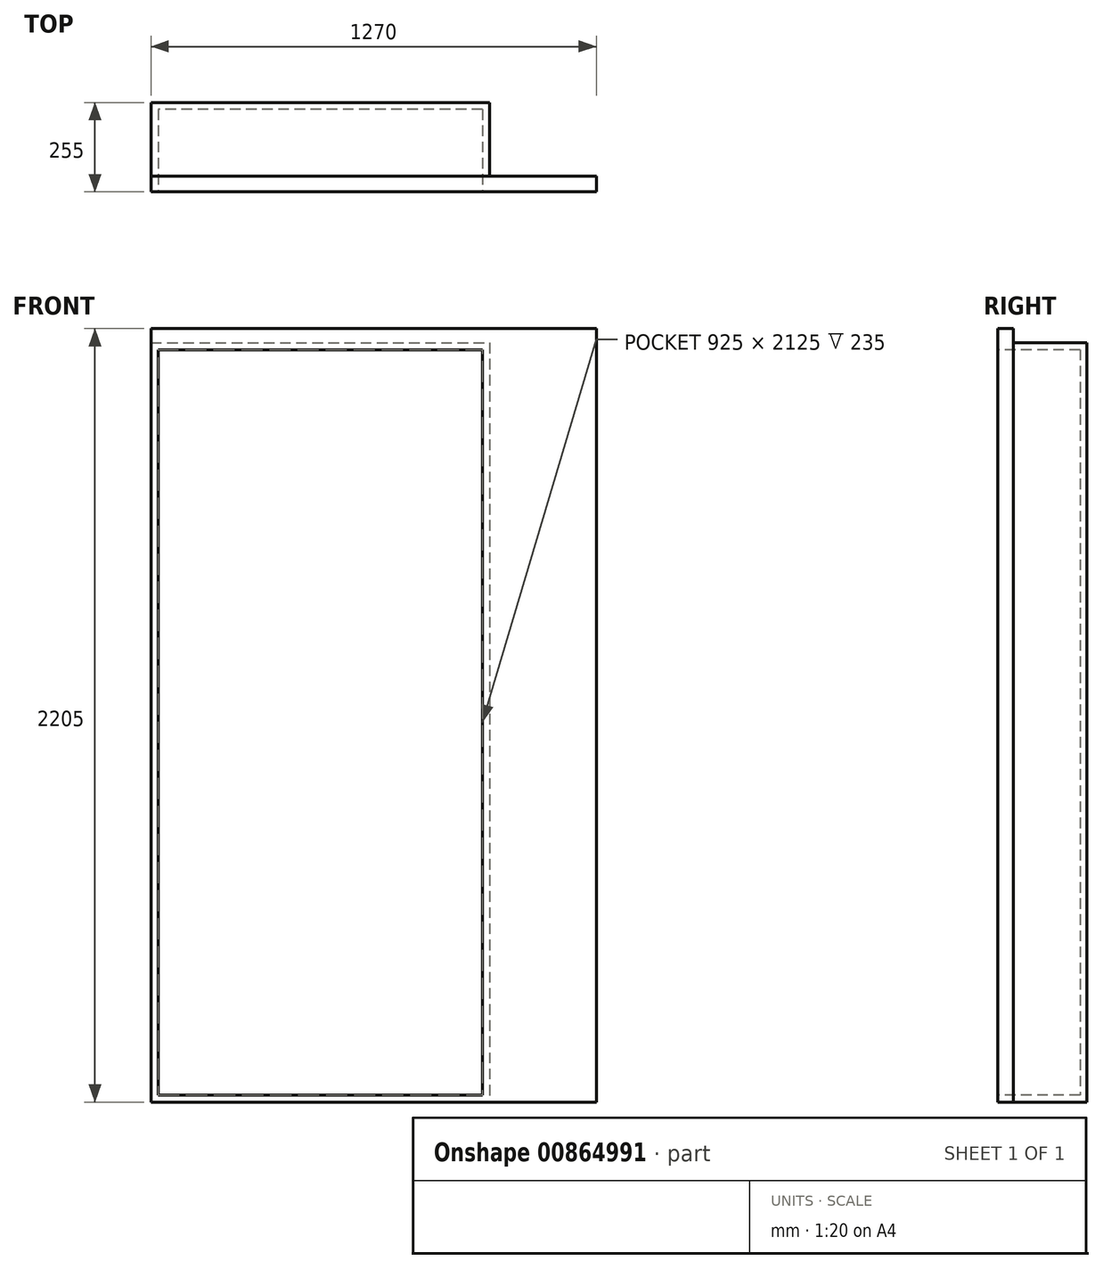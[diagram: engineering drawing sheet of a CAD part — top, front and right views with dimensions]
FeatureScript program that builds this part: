
annotation { "Feature Type Name" : "Feature", "Feature Type Description" : "" }
export const myFeature = defineFeature(function(context is Context, id is Id, definition is map)
    precondition{}
    {
        {
            var Q0;
            Q0=qCreatedBy(makeId("Top.planeOp"),FACE);
            var sketch = newSketch(context, id + "F0", { "sketchPlane" : qUnion([Q0])});
            skLineSegment(sketch, "E0", {"start": v(0, 0) * mm, "end": v(0, 255) * mm});
            skLineSegment(sketch, "E1", {"start": v(0, 255) * mm, "end": v(965, 255) * mm});
            skLineSegment(sketch, "E2", {"start": v(965, 255) * mm, "end": v(965, 45) * mm});
            skLineSegment(sketch, "E3", {"start": v(965, 45) * mm, "end": v(1270, 45) * mm});
            skLineSegment(sketch, "E4", {"start": v(1270, 45) * mm, "end": v(1270, 0) * mm});
            skLineSegment(sketch, "E5", {"start": v(1270, 0) * mm, "end": v(0, 0) * mm});
            skSolve(sketch);
        }
        {
            var Q0;
            Q0 = qSketchRegion(id + "F0", true);
            extrude(context, id + "F1", {"entities" : qUnion([Q0]), "depth" : (2205 - 40) * mm, "offsetDistance" : 25 * mm});
        }
        {
            var Q0;
            Q0=makeQuery(id+"F1.opExtrude","CAP_FACE",FACE,{"disambiguationData":[OSD([sQuery(id+"F0.wireOp",EDGE,"E0"),sQuery(id+"F0.wireOp",EDGE,"E1"),sQuery(id+"F0.wireOp",EDGE,"E2"),sQuery(id+"F0.wireOp",EDGE,"E3"),sQuery(id+"F0.wireOp",EDGE,"E4"),sQuery(id+"F0.wireOp",EDGE,"E5")])],"isStart":false});
            var sketch = newSketch(context, id + "F2", { "sketchPlane" : qUnion([Q0])});
            skLineSegment(sketch, "E6.bottom", {"start": v(1270, 45) * mm, "end": v(0, 45) * mm});
            skLineSegment(sketch, "E6.top", {"start": v(1270, 0) * mm, "end": v(0, 0) * mm});
            skLineSegment(sketch, "E6.left", {"start": v(1270, 45) * mm, "end": v(1270, 0) * mm});
            skLineSegment(sketch, "E6.right", {"start": v(0, 45) * mm, "end": v(0, 0) * mm});
            skSolve(sketch);
        }
        {
            var Q0;
            Q0 = qSketchRegion(id + "F2", true);
            extrude(context, id + "F3", {"entities" : qUnion([Q0]), "operationType" : NewBodyOperationType.ADD, "depth" : 40 * mm, "offsetDistance" : 25 * mm});
        }
        {
            var Q0;
            Q0=makeQuery(id+"F3.boolean.opBoolean","MERGE",FACE,{"derivedFrom":[makeQuery(id+"F1.opExtrude","SWEPT_FACE",FACE,{"disambiguationData":[OSD([sQuery(id+"F0.wireOp",EDGE,"E5")])]}),makeQuery(id+"F3.opExtrude","SWEPT_FACE",FACE,{"disambiguationData":[OSD([sQuery(id+"F2.wireOp",EDGE,"E6.top")])]})]});
            var sketch = newSketch(context, id + "F4", { "sketchPlane" : qUnion([Q0])});
            skLineSegment(sketch, "E7.0", {"start": v(945, 20) * mm, "end": v(20, 20) * mm});
            skLineSegment(sketch, "E7.1", {"start": v(945, 2145) * mm, "end": v(945, 20) * mm});
            skLineSegment(sketch, "E7.2", {"start": v(20, 2145) * mm, "end": v(945, 2145) * mm});
            skLineSegment(sketch, "E7.3", {"start": v(20, 20) * mm, "end": v(20, 2145) * mm});
            skSolve(sketch);
        }
        {
            var Q0;
            Q0 = qSketchRegion(id + "F4", true);
            extrude(context, id + "F5", {"entities" : qUnion([Q0]), "operationType" : NewBodyOperationType.REMOVE, "oppositeDirection" : true, "depth" : 235 * mm, "offsetDistance" : 25 * mm});
        }
    });
